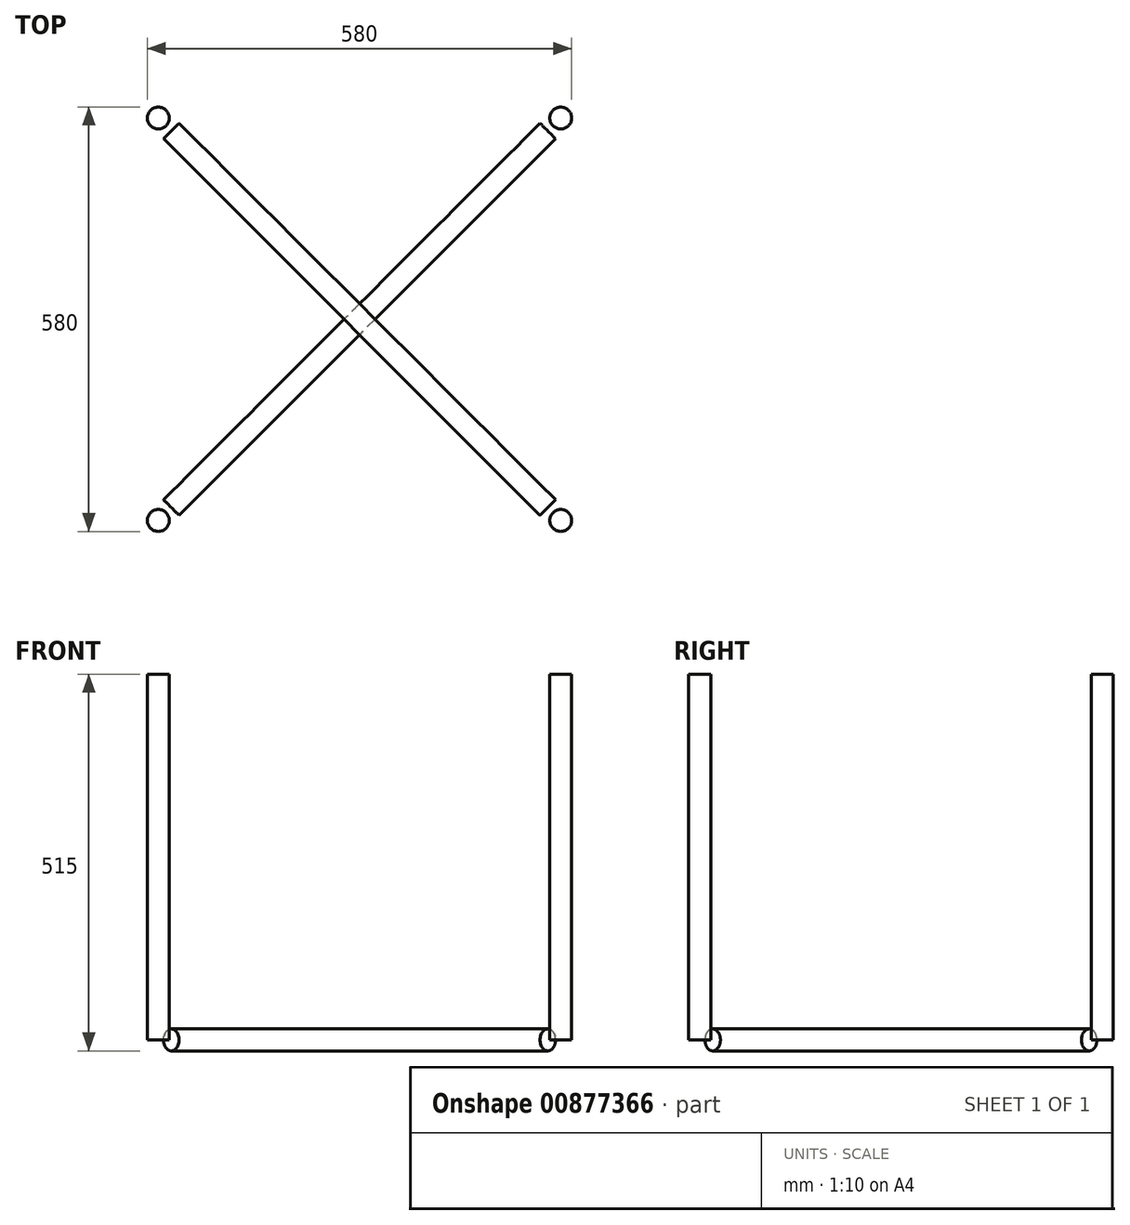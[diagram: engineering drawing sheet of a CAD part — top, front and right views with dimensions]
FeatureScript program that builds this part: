
annotation { "Feature Type Name" : "Feature", "Feature Type Description" : "" }
export const myFeature = defineFeature(function(context is Context, id is Id, definition is map)
    precondition{}
    {
        {
            assignVariable(context, id + "F0", {"name" : "height", "anyValue" : 500});
        }
        {
            var Q0;
            Q0=qCreatedBy(makeId("Top.planeOp"),FACE);
            var sketch = newSketch(context, id + "F1", { "sketchPlane" : qUnion([Q0])});
            skLineSegment(sketch, "E0.bottom", {"start": v(-275, 275) * mm, "end": v(275, 275) * mm, "construction": true});
            skLineSegment(sketch, "E0.top", {"start": v(-275, -275) * mm, "end": v(275, -275) * mm, "construction": true});
            skLineSegment(sketch, "E0.left", {"start": v(-275, 275) * mm, "end": v(-275, -275) * mm, "construction": true});
            skLineSegment(sketch, "E0.right", {"start": v(275, 275) * mm, "end": v(275, -275) * mm, "construction": true});
            skPoint(sketch, "E0.middle", {"position": v(0, 0) * mm});
            skCircle(sketch, "E1", {"center": v(-275, 275) * mm, "radius": 15 * mm});
            skCircle(sketch, "E2", {"center": v(275, 275) * mm, "radius": 15 * mm});
            skCircle(sketch, "E3", {"center": v(-275, -275) * mm, "radius": 15 * mm});
            skCircle(sketch, "E4", {"center": v(275, -275) * mm, "radius": 15 * mm});
            skLineSegment(sketch, "E5", {"start": v(-257.32, 257.32) * mm, "end": v(257.32, -257.32) * mm});
            skLineSegment(sketch, "E6", {"start": v(-257.32, 257.32) * mm, "end": v(-275, 275) * mm, "construction": true});
            skLineSegment(sketch, "E7", {"start": v(257.32, -257.32) * mm, "end": v(275, -275) * mm, "construction": true});
            skSolve(sketch);
        }
        {
            var Q0;
            Q0 = qSketchRegion(id + "F1", true);
            extrude(context, id + "F2", {"entities" : qUnion([Q0]), "depth" : (getVariable(context, 'height')) * mm, "offsetDistance" : 25 * mm});
        }
        {
            var Q0;
            Q0=sQuery(id+"F1.wireOp",EDGE,"E5");
            var Q1;
            Q1=sQuery(id+"F1.wireOp",VERTEX,"E5.start");
            cPlane(context, id + "F3", {"entities" : qUnion([Q0, Q1]), "cplaneType" : CPlaneType.LINE_POINT, "offset" : 25 * mm, "width" : 150 * mm, "height" : 150 * mm});
        }
        {
            var Q0;
            Q0=qCreatedBy(id+"F3.planeOp",FACE);
            var sketch = newSketch(context, id + "F4", { "sketchPlane" : qUnion([Q0])});
            skCircle(sketch, "E8", {"center": v(0, 0) * mm, "radius": 15 * mm});
            skSolve(sketch);
        }
        {
            var Q0;
            Q0=makeQuery(id+"F4.imprint","IMPRINT",FACE,{"disambiguationData":[TD([[makeQuery(id+"F4.imprint","IMPRINT",EDGE,{"derivedFrom":sQuery(id+"F4.wireOp",EDGE,"E8")}),1.0]])]});
            var Q1;
            Q1=sQuery(id+"F1.wireOp",EDGE,"E5");
            sweep(context, id + "F5", {"profiles" : qUnion([Q0]), "path" : qUnion([Q1])});
        }
        {
            var Q0;
            Q0=makeQuery(id+"F5.opSweep","SWEPT_BODY",BODY,{"disambiguationData":[OSD([sQuery(id+"F1.wireOp",EDGE,"E5"),sQuery(id+"F4.wireOp",EDGE,"E8")])]});
            var Q1;
            Q1=qCreatedBy(makeId("Right.planeOp"),FACE);
            mirror(context, id + "F6", {"operationType" : NewBodyOperationType.ADD, "entities" : qUnion([Q0]), "mirrorPlane" : qUnion([Q1])});
        }
    });
